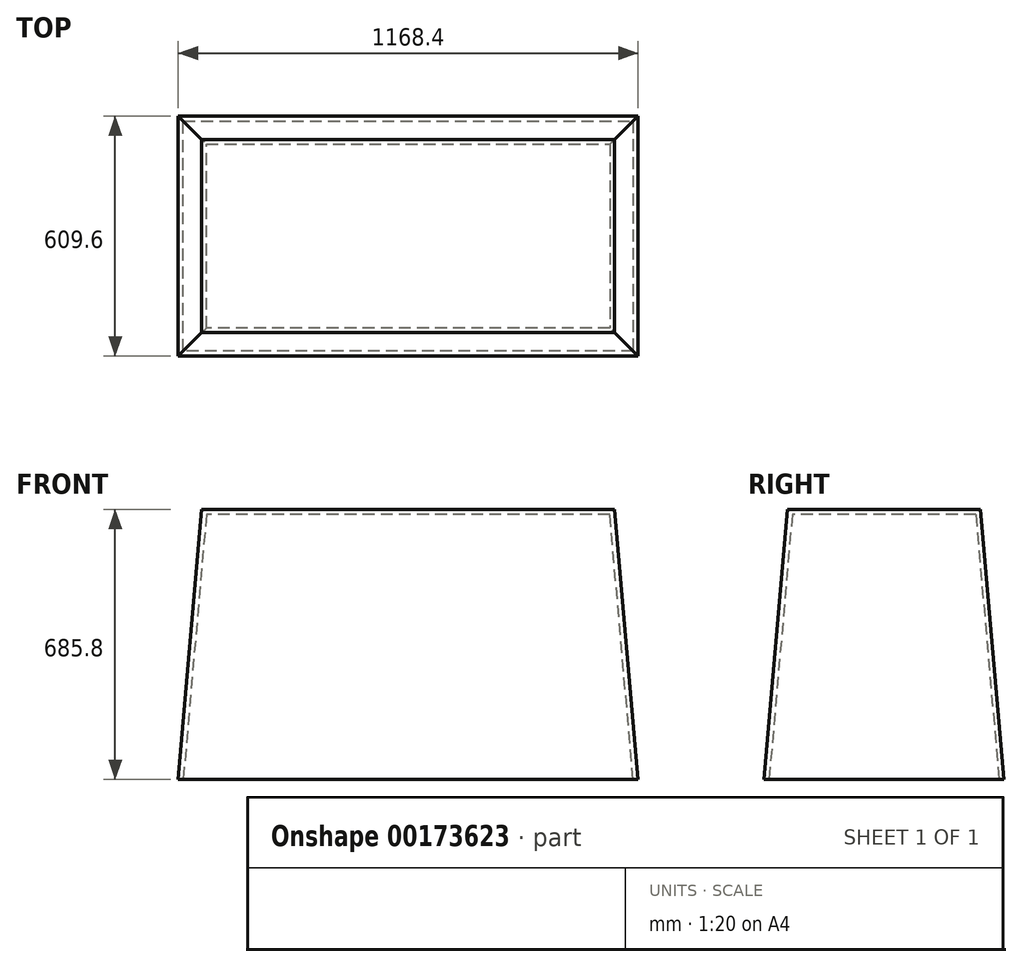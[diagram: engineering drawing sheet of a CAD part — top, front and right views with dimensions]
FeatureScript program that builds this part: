
annotation { "Feature Type Name" : "Feature", "Feature Type Description" : "" }
export const myFeature = defineFeature(function(context is Context, id is Id, definition is map)
    precondition{}
    {
        {
            var Q0;
            Q0=qCreatedBy(makeId("Top.planeOp"),FACE);
            var sketch = newSketch(context, id + "F0", { "sketchPlane" : qUnion([Q0])});
            skLineSegment(sketch, "E0.bottom", {"start": v(584.2, -304.8) * mm, "end": v(-584.2, -304.8) * mm});
            skLineSegment(sketch, "E0.top", {"start": v(584.2, 304.8) * mm, "end": v(-584.2, 304.8) * mm});
            skLineSegment(sketch, "E0.left", {"start": v(584.2, -304.8) * mm, "end": v(584.2, 304.8) * mm});
            skLineSegment(sketch, "E0.right", {"start": v(-584.2, -304.8) * mm, "end": v(-584.2, 304.8) * mm});
            skPoint(sketch, "E0.middle", {"position": v(0, 0) * mm});
            skSolve(sketch);
        }
        {
            var Q0;
            Q0=makeQuery(id+"F0.imprint","IMPRINT",FACE,{"disambiguationData":[TD([[makeQuery(id+"F0.imprint","IMPRINT",EDGE,{"derivedFrom":sQuery(id+"F0.wireOp",EDGE,"E0.bottom")}),-1.0]])]});
            extrude(context, id + "F1", {"entities" : qUnion([Q0]), "depth" : 685.8 * mm, "hasDraft" : true, "draftAngle" : 5 * degree, "draftPullDirection" : true});
        }
        {
            var Q0;
            Q0=makeQuery(id+"F1.opExtrude","CAP_FACE",FACE,{"disambiguationData":[OSD([sQuery(id+"F0.wireOp",EDGE,"E0.bottom"),sQuery(id+"F0.wireOp",EDGE,"E0.top"),sQuery(id+"F0.wireOp",EDGE,"E0.left"),sQuery(id+"F0.wireOp",EDGE,"E0.right")])],"isStart":true});
            shell(context, id + "F2", {"entities" : qUnion([Q0]), "thickness" : 12.7 * mm});
        }
    });
